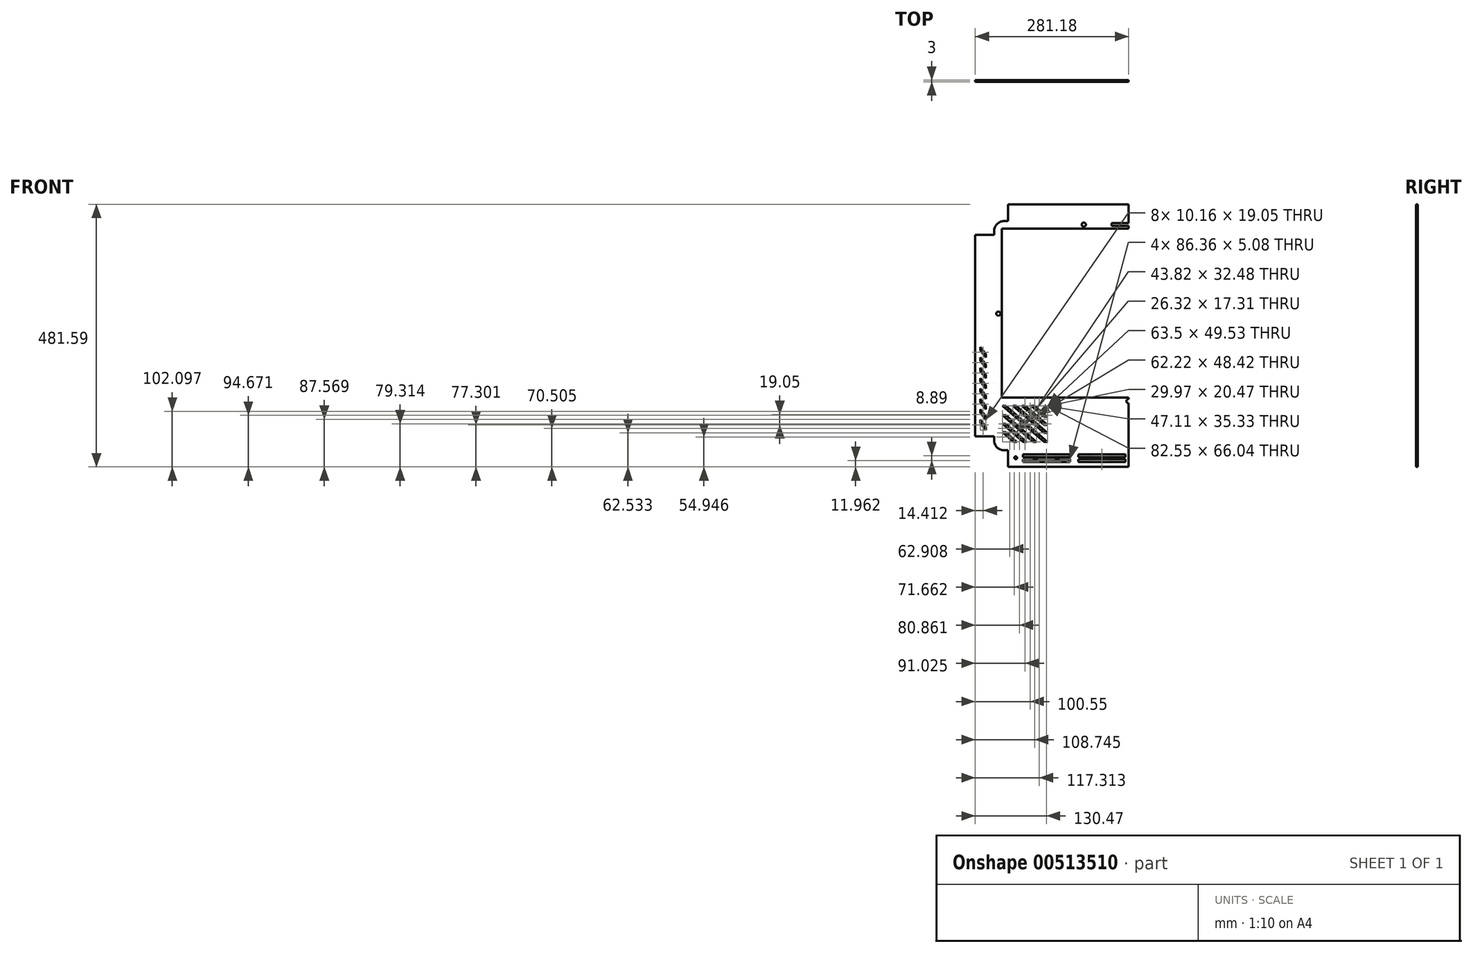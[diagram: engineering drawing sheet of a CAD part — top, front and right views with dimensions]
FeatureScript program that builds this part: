
annotation { "Feature Type Name" : "Feature", "Feature Type Description" : "" }
export const myFeature = defineFeature(function(context is Context, id is Id, definition is map)
    precondition{}
    {
        {
            var Q0;
            Q0=qCreatedBy(makeId("Front.planeOp"),FACE);
            var sketch = newSketch(context, id + "F0", { "sketchPlane" : qUnion([Q0])});
            skPoint(sketch, "E0.middle", {"position": v(184.66, 417.39) * mm});
            skPoint(sketch, "E1.visualSharp", {"position": v(-246.57, 210.48) * mm});
            skPoint(sketch, "E2.visualSharp", {"position": v(-246.57, -212.69) * mm});
            skPoint(sketch, "E3.visualSharp", {"position": v(-242.5, 203.87) * mm});
            skLineSegment(sketch, "E4.bottom", {"start": v(-280.86, 185.08) * mm, "end": v(-246.57, 185.08) * mm});
            skLineSegment(sketch, "E4.top", {"start": v(-280.86, -184.75) * mm, "end": v(-246.57, -184.75) * mm});
            skLineSegment(sketch, "E4.left", {"start": v(-280.86, 185.08) * mm, "end": v(-280.86, -184.75) * mm});
            skLineSegment(sketch, "E4.right", {"start": v(-246.57, 185.08) * mm, "end": v(-246.57, -184.75) * mm});
            skLineSegment(sketch, "E5.bottom", {"start": v(-221.17, 240.96) * mm, "end": v(0.32, 240.96) * mm});
            skLineSegment(sketch, "E5.left", {"start": v(-221.17, 240.96) * mm, "end": v(-221.17, 210.48) * mm});
            skLineSegment(sketch, "E6.bottom", {"start": v(-221.17, -210.15) * mm, "end": v(0.32, -210.15) * mm});
            skLineSegment(sketch, "E6.top", {"start": v(-221.17, -240.63) * mm, "end": v(0.32, -240.63) * mm});
            skLineSegment(sketch, "E6.left", {"start": v(-221.17, -210.15) * mm, "end": v(-221.17, -240.63) * mm});
            skLineSegment(sketch, "E7.bottom", {"start": v(-202.12, 210.48) * mm, "end": v(0.32, 210.48) * mm});
            skLineSegment(sketch, "E8", {"start": v(0.32, 240.96) * mm, "end": v(0.32, 210.48) * mm});
            skLineSegment(sketch, "E9", {"start": v(0.32, -240.63) * mm, "end": v(0.32, -210.15) * mm});
            skLineSegment(sketch, "E10.bottom", {"start": v(0.32, -210.15) * mm, "end": v(-227.52, -210.15) * mm});
            skLineSegment(sketch, "E10.top", {"start": v(0.32, 210.48) * mm, "end": v(-227.52, 210.48) * mm});
            skLineSegment(sketch, "E10.left", {"start": v(0.32, -210.15) * mm, "end": v(0.32, 210.48) * mm});
            skLineSegment(sketch, "E10.right", {"start": v(-246.57, -191.1) * mm, "end": v(-246.57, 191.43) * mm});
            skArc(sketch, "E11.filletArc", {"start": v(-227.52, 210.48) * mm, "mid": v(-241, 204.9) * mm, "end": v(-246.57, 191.43) * mm});
            skPoint(sketch, "E12.visualSharp", {"position": v(-246.57, -210.15) * mm});
            skArc(sketch, "E12.filletArc", {"start": v(-246.57, -191.1) * mm, "mid": v(-241, -204.57) * mm, "end": v(-227.52, -210.15) * mm});
            skSolve(sketch);
        }
        {
            var Q0;
            Q0 = qSketchRegion(id + "F0", true);
            extrude(context, id + "F1", {"entities" : qUnion([Q0]), "depth" : 3 * mm, "offsetDistance" : 25.4 * mm});
        }
        {
            var Q0;
            Q0=qCreatedBy(makeId("Front.planeOp"),FACE);
            var sketch = newSketch(context, id + "F2", { "sketchPlane" : qUnion([Q0])});
            skLineSegment(sketch, "E13.bottom", {"start": v(-232.35, 196.25) * mm, "end": v(0, 196.25) * mm});
            skLineSegment(sketch, "E13.top", {"start": v(-232.35, -113.63) * mm, "end": v(0, -113.63) * mm});
            skLineSegment(sketch, "E13.left", {"start": v(-232.35, 196.25) * mm, "end": v(-232.35, -113.63) * mm});
            skLineSegment(sketch, "E13.right", {"start": v(0, 196.25) * mm, "end": v(0, -113.63) * mm});
            skLineSegment(sketch, "E14.bottom", {"start": v(-19.78, 196.25) * mm, "end": v(22.36, 196.25) * mm});
            skLineSegment(sketch, "E14.top", {"start": v(-19.78, -113.63) * mm, "end": v(22.36, -113.63) * mm});
            skLineSegment(sketch, "E14.left", {"start": v(-19.78, 196.25) * mm, "end": v(-19.78, -113.63) * mm});
            skLineSegment(sketch, "E14.right", {"start": v(22.36, 196.25) * mm, "end": v(22.36, -113.63) * mm});
            skLineSegment(sketch, "E15", {"start": v(-271.53, -153.8) * mm, "end": v(-271.53, -160.15) * mm});
            skLineSegment(sketch, "E16", {"start": v(-271.53, -160.15) * mm, "end": v(-261.37, -172.85) * mm});
            skLineSegment(sketch, "E17", {"start": v(-261.37, -172.85) * mm, "end": v(-261.37, -166.5) * mm});
            skLineSegment(sketch, "E18", {"start": v(-261.37, -166.5) * mm, "end": v(-271.53, -153.8) * mm});
            skLineSegment(sketch, "E19", {"start": v(-271.53, -141.1) * mm, "end": v(-271.53, -134.75) * mm});
            skLineSegment(sketch, "E20", {"start": v(-271.53, -134.75) * mm, "end": v(-261.37, -147.45) * mm});
            skLineSegment(sketch, "E21", {"start": v(-261.37, -147.45) * mm, "end": v(-261.37, -153.8) * mm});
            skLineSegment(sketch, "E22", {"start": v(-261.37, -153.8) * mm, "end": v(-271.53, -141.1) * mm});
            skLineSegment(sketch, "E23", {"start": v(-261.37, -134.75) * mm, "end": v(-261.37, -128.4) * mm});
            skLineSegment(sketch, "E24", {"start": v(-261.37, -128.4) * mm, "end": v(-271.53, -115.7) * mm});
            skLineSegment(sketch, "E25", {"start": v(-271.53, -115.7) * mm, "end": v(-271.53, -122.05) * mm});
            skLineSegment(sketch, "E26", {"start": v(-271.53, -122.05) * mm, "end": v(-261.37, -134.75) * mm});
            skLineSegment(sketch, "E27", {"start": v(-261.37, -115.7) * mm, "end": v(-271.53, -103) * mm});
            skLineSegment(sketch, "E28", {"start": v(-271.53, -103) * mm, "end": v(-271.53, -96.65) * mm});
            skLineSegment(sketch, "E29", {"start": v(-271.53, -96.65) * mm, "end": v(-261.37, -109.35) * mm});
            skLineSegment(sketch, "E30", {"start": v(-261.37, -109.35) * mm, "end": v(-261.37, -115.7) * mm});
            skLineSegment(sketch, "E31", {"start": v(-261.37, -96.65) * mm, "end": v(-271.53, -83.95) * mm});
            skLineSegment(sketch, "E32", {"start": v(-271.53, -83.95) * mm, "end": v(-271.53, -77.6) * mm});
            skLineSegment(sketch, "E33", {"start": v(-271.53, -77.6) * mm, "end": v(-261.37, -90.3) * mm});
            skLineSegment(sketch, "E34", {"start": v(-261.37, -90.3) * mm, "end": v(-261.37, -96.65) * mm});
            skLineSegment(sketch, "E35", {"start": v(-261.37, -77.6) * mm, "end": v(-271.53, -64.9) * mm});
            skLineSegment(sketch, "E36", {"start": v(-271.53, -64.9) * mm, "end": v(-271.53, -58.55) * mm});
            skLineSegment(sketch, "E37", {"start": v(-271.53, -58.55) * mm, "end": v(-261.37, -71.25) * mm});
            skLineSegment(sketch, "E38", {"start": v(-261.37, -71.25) * mm, "end": v(-261.37, -77.6) * mm});
            skLineSegment(sketch, "E39", {"start": v(-261.37, -58.55) * mm, "end": v(-271.53, -45.85) * mm});
            skLineSegment(sketch, "E40", {"start": v(-271.53, -45.85) * mm, "end": v(-271.53, -39.5) * mm});
            skLineSegment(sketch, "E41", {"start": v(-271.53, -39.5) * mm, "end": v(-261.37, -52.2) * mm});
            skLineSegment(sketch, "E42", {"start": v(-261.37, -52.2) * mm, "end": v(-261.37, -58.55) * mm});
            skLineSegment(sketch, "E43", {"start": v(-261.37, -39.5) * mm, "end": v(-271.53, -26.8) * mm});
            skLineSegment(sketch, "E44", {"start": v(-271.53, -26.8) * mm, "end": v(-271.53, -20.45) * mm});
            skLineSegment(sketch, "E45", {"start": v(-271.53, -20.45) * mm, "end": v(-261.37, -33.15) * mm});
            skLineSegment(sketch, "E46", {"start": v(-261.37, -33.15) * mm, "end": v(-261.37, -39.5) * mm});
            skLineSegment(sketch, "E47", {"start": v(-193.57, -231.2) * mm, "end": v(-107.21, -231.2) * mm});
            skLineSegment(sketch, "E48", {"start": v(-107.21, -231.2) * mm, "end": v(-107.21, -226.13) * mm});
            skLineSegment(sketch, "E49", {"start": v(-107.21, -226.13) * mm, "end": v(-193.57, -226.13) * mm});
            skLineSegment(sketch, "E50", {"start": v(-193.57, -226.13) * mm, "end": v(-193.57, -231.2) * mm});
            skLineSegment(sketch, "E51", {"start": v(-193.57, -222.32) * mm, "end": v(-193.57, -217.24) * mm});
            skLineSegment(sketch, "E52", {"start": v(-193.57, -217.24) * mm, "end": v(-107.21, -217.24) * mm});
            skLineSegment(sketch, "E53", {"start": v(-107.21, -217.24) * mm, "end": v(-107.21, -222.32) * mm});
            skLineSegment(sketch, "E54", {"start": v(-107.21, -222.32) * mm, "end": v(-193.57, -222.32) * mm});
            skLineSegment(sketch, "E55", {"start": v(-91.97, -217.24) * mm, "end": v(-91.97, -222.32) * mm});
            skLineSegment(sketch, "E56", {"start": v(-91.97, -222.32) * mm, "end": v(-5.61, -222.32) * mm});
            skLineSegment(sketch, "E57", {"start": v(-5.61, -222.32) * mm, "end": v(-5.61, -217.24) * mm});
            skLineSegment(sketch, "E58", {"start": v(-5.61, -217.24) * mm, "end": v(-91.97, -217.24) * mm});
            skLineSegment(sketch, "E59", {"start": v(-91.97, -226.13) * mm, "end": v(-91.97, -231.2) * mm});
            skLineSegment(sketch, "E60", {"start": v(-91.97, -231.2) * mm, "end": v(-5.61, -231.2) * mm});
            skLineSegment(sketch, "E61", {"start": v(-5.61, -231.2) * mm, "end": v(-5.61, -226.13) * mm});
            skLineSegment(sketch, "E62", {"start": v(-5.61, -226.13) * mm, "end": v(-91.97, -226.13) * mm});
            skCircle(sketch, "E63", {"center": v(-206.76, -223.78) * mm, "radius": 2.5 * mm});
            skCircle(sketch, "E64", {"center": v(-81.98, 203.87) * mm, "radius": 3.81 * mm});
            skCircle(sketch, "E65", {"center": v(-238.7, 40.66) * mm, "radius": 3.81 * mm});
            skCircle(sketch, "E66", {"center": v(0, -119.98) * mm, "radius": 3.81 * mm});
            skLineSegment(sketch, "E67.bottom", {"start": v(-31.18, 206.41) * mm, "end": v(25.84, 206.41) * mm});
            skLineSegment(sketch, "E67.top", {"start": v(-31.18, 201.33) * mm, "end": v(25.84, 201.33) * mm});
            skLineSegment(sketch, "E67.left", {"start": v(-31.18, 206.41) * mm, "end": v(-31.18, 201.33) * mm});
            skLineSegment(sketch, "E67.right", {"start": v(25.84, 206.41) * mm, "end": v(25.84, 201.33) * mm});
            skSolve(sketch);
        }
        {
            var Q0;
            Q0 = qSketchRegion(id + "F2", true);
            extrude(context, id + "F3", {"entities" : qUnion([Q0]), "operationType" : NewBodyOperationType.REMOVE, "depth" : 25.4 * mm, "offsetDistance" : 25.4 * mm});
        }
        {
            var Q0;
            Q0=qCreatedBy(makeId("Front.planeOp"),FACE);
            var sketch = newSketch(context, id + "F4", { "sketchPlane" : qUnion([Q0])});
            skLineSegment(sketch, "E68", {"start": v(-231.11, -128.3) * mm, "end": v(-224.76, -128.3) * mm});
            skLineSegment(sketch, "E69", {"start": v(-224.76, -128.3) * mm, "end": v(-148.56, -194.34) * mm});
            skLineSegment(sketch, "E70", {"start": v(-148.56, -194.34) * mm, "end": v(-154.91, -194.34) * mm});
            skLineSegment(sketch, "E71", {"start": v(-154.91, -194.34) * mm, "end": v(-231.11, -128.3) * mm});
            skLineSegment(sketch, "E72", {"start": v(-212.06, -128.3) * mm, "end": v(-205.71, -128.3) * mm});
            skLineSegment(sketch, "E73", {"start": v(-148.56, -177.83) * mm, "end": v(-154.91, -177.83) * mm});
            skLineSegment(sketch, "E74", {"start": v(-154.91, -177.83) * mm, "end": v(-212.06, -128.3) * mm});
            skLineSegment(sketch, "E75", {"start": v(-205.71, -128.3) * mm, "end": v(-148.56, -177.83) * mm});
            skLineSegment(sketch, "E76", {"start": v(-231.11, -145.91) * mm, "end": v(-224.76, -145.91) * mm});
            skLineSegment(sketch, "E77", {"start": v(-224.76, -145.91) * mm, "end": v(-168.89, -194.34) * mm});
            skLineSegment(sketch, "E78", {"start": v(-168.89, -194.34) * mm, "end": v(-175.24, -194.34) * mm});
            skLineSegment(sketch, "E79", {"start": v(-175.24, -194.34) * mm, "end": v(-231.11, -145.91) * mm});
            skLineSegment(sketch, "E80", {"start": v(-231.11, -161.86) * mm, "end": v(-224.76, -161.86) * mm});
            skLineSegment(sketch, "E81", {"start": v(-224.76, -161.86) * mm, "end": v(-187.29, -194.34) * mm});
            skLineSegment(sketch, "E82", {"start": v(-187.29, -194.34) * mm, "end": v(-193.64, -194.34) * mm});
            skLineSegment(sketch, "E83", {"start": v(-193.64, -194.34) * mm, "end": v(-231.11, -161.86) * mm});
            skLineSegment(sketch, "E84", {"start": v(-231.11, -177.03) * mm, "end": v(-224.76, -177.03) * mm});
            skLineSegment(sketch, "E85", {"start": v(-224.76, -177.03) * mm, "end": v(-204.8, -194.34) * mm});
            skLineSegment(sketch, "E86", {"start": v(-204.8, -194.34) * mm, "end": v(-211.14, -194.34) * mm});
            skLineSegment(sketch, "E87", {"start": v(-211.14, -194.34) * mm, "end": v(-231.11, -177.03) * mm});
            skLineSegment(sketch, "E88", {"start": v(-148.56, -163.62) * mm, "end": v(-154.91, -163.62) * mm});
            skLineSegment(sketch, "E89", {"start": v(-154.91, -163.62) * mm, "end": v(-195.67, -128.3) * mm});
            skLineSegment(sketch, "E90", {"start": v(-195.67, -128.3) * mm, "end": v(-189.32, -128.3) * mm});
            skLineSegment(sketch, "E91", {"start": v(-189.32, -128.3) * mm, "end": v(-148.56, -163.62) * mm});
            skLineSegment(sketch, "E92", {"start": v(-148.56, -148.77) * mm, "end": v(-154.91, -148.77) * mm});
            skLineSegment(sketch, "E93", {"start": v(-154.91, -148.77) * mm, "end": v(-178.53, -128.3) * mm});
            skLineSegment(sketch, "E94", {"start": v(-178.53, -128.3) * mm, "end": v(-172.18, -128.3) * mm});
            skLineSegment(sketch, "E95", {"start": v(-172.18, -128.3) * mm, "end": v(-148.56, -148.77) * mm});
            skSolve(sketch);
        }
        {
            var Q0;
            Q0 = qSketchRegion(id + "F4", true);
            extrude(context, id + "F5", {"entities" : qUnion([Q0]), "operationType" : NewBodyOperationType.REMOVE, "depth" : 25.4 * mm, "offsetDistance" : 25.4 * mm});
        }
    });
